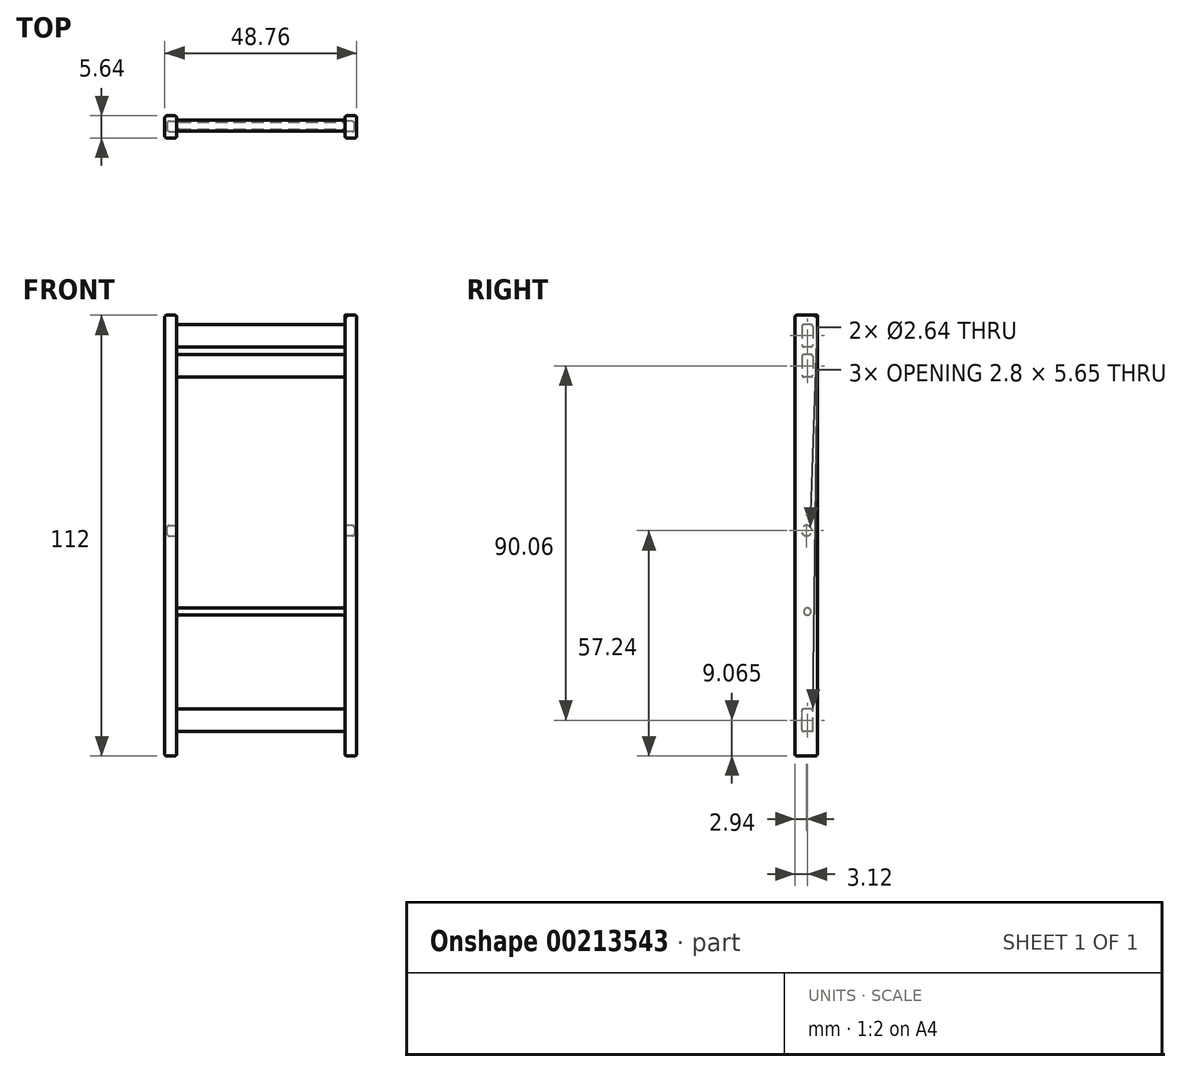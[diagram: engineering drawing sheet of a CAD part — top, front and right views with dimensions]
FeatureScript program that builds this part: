
annotation { "Feature Type Name" : "Feature", "Feature Type Description" : "" }
export const myFeature = defineFeature(function(context is Context, id is Id, definition is map)
    precondition{}
    {
        {
            var Q0;
            Q0=qCreatedBy(makeId("Right.planeOp"),FACE);
            var sketch = newSketch(context, id + "F0", { "sketchPlane" : qUnion([Q0])});
            skLineSegment(sketch, "E0.bottom", {"start": v(2.82, -56) * mm, "end": v(-2.82, -56) * mm});
            skLineSegment(sketch, "E0.top", {"start": v(2.82, 56) * mm, "end": v(-2.82, 56) * mm});
            skLineSegment(sketch, "E0.left", {"start": v(2.82, -56) * mm, "end": v(2.82, 56) * mm});
            skLineSegment(sketch, "E0.right", {"start": v(-2.82, -56) * mm, "end": v(-2.82, 56) * mm});
            skPoint(sketch, "E0.middle", {"position": v(0, 0) * mm});
            skSolve(sketch);
        }
        {
            var Q0;
            Q0=makeQuery(id+"F0.imprint","IMPRINT",FACE,{"disambiguationData":[TD([[makeQuery(id+"F0.imprint","IMPRINT",EDGE,{"derivedFrom":sQuery(id+"F0.wireOp",EDGE,"E0.bottom")}),-1.0]])]});
            extrude(context, id + "F1", {"entities" : qUnion([Q0]), "depth" : 3 * mm});
        }
        {
            var Q0;
            Q0=makeQuery(id+"F1.opExtrude","CAP_FACE",FACE,{"disambiguationData":[OSD([sQuery(id+"F0.wireOp",EDGE,"E0.bottom"),sQuery(id+"F0.wireOp",EDGE,"E0.top"),sQuery(id+"F0.wireOp",EDGE,"E0.left"),sQuery(id+"F0.wireOp",EDGE,"E0.right")])],"isStart":true});
            var sketch = newSketch(context, id + "F2", { "sketchPlane" : qUnion([Q0])});
            skLineSegment(sketch, "E1.bottom", {"start": v(-1.7, 53.6) * mm, "end": v(1.1, 53.6) * mm});
            skLineSegment(sketch, "E1.top", {"start": v(-1.7, 47.95) * mm, "end": v(1.1, 47.95) * mm});
            skLineSegment(sketch, "E1.left", {"start": v(-1.7, 53.6) * mm, "end": v(-1.7, 47.95) * mm});
            skLineSegment(sketch, "E1.right", {"start": v(1.1, 53.6) * mm, "end": v(1.1, 47.95) * mm});
            skLineSegment(sketch, "E2.bottom", {"start": v(-1.7, 45.95) * mm, "end": v(1.1, 45.95) * mm});
            skLineSegment(sketch, "E2.top", {"start": v(-1.7, 40.3) * mm, "end": v(1.1, 40.3) * mm});
            skLineSegment(sketch, "E2.left", {"start": v(-1.7, 45.95) * mm, "end": v(-1.7, 40.3) * mm});
            skLineSegment(sketch, "E2.right", {"start": v(1.1, 45.95) * mm, "end": v(1.1, 40.3) * mm});
            skLineSegment(sketch, "E3.bottom", {"start": v(-1.7, -49.76) * mm, "end": v(1.1, -49.76) * mm});
            skLineSegment(sketch, "E3.top", {"start": v(-1.7, -44.1) * mm, "end": v(1.1, -44.1) * mm});
            skLineSegment(sketch, "E3.left", {"start": v(-1.7, -49.76) * mm, "end": v(-1.7, -44.11) * mm});
            skLineSegment(sketch, "E3.right", {"start": v(1.1, -49.76) * mm, "end": v(1.1, -44.1) * mm});
            skCircle(sketch, "E4", {"center": v(-0.32, -19.3) * mm, "radius": 0.9 * mm});
            skSolve(sketch);
        }
        {
            var Q0;
            Q0 = qSketchRegion(id + "F2", true);
            extrude(context, id + "F3", {"entities" : qUnion([Q0]), "operationType" : NewBodyOperationType.ADD, "depth" : 42.76 * mm});
        }
        {
            var Q0;
            Q0=makeQuery(id+"F3.opExtrude","CAP_FACE",FACE,{"disambiguationData":[OSD([sQuery(id+"F2.wireOp",EDGE,"E1.bottom"),sQuery(id+"F2.wireOp",EDGE,"E1.top"),sQuery(id+"F2.wireOp",EDGE,"E1.left"),sQuery(id+"F2.wireOp",EDGE,"E1.right")])],"isStart":false});
            var sketch = newSketch(context, id + "F4", { "sketchPlane" : qUnion([Q0])});
            skLineSegment(sketch, "E5.bottom", {"start": v(-2.82, 56) * mm, "end": v(2.82, 56) * mm});
            skLineSegment(sketch, "E5.top", {"start": v(-2.82, -56) * mm, "end": v(2.82, -56) * mm});
            skLineSegment(sketch, "E5.left", {"start": v(-2.82, 56) * mm, "end": v(-2.82, -56) * mm});
            skLineSegment(sketch, "E5.right", {"start": v(2.82, 56) * mm, "end": v(2.82, -56) * mm});
            skSolve(sketch);
        }
        {
            var Q0;
            Q0 = qSketchRegion(id + "F4", true);
            extrude(context, id + "F5", {"entities" : qUnion([Q0]), "operationType" : NewBodyOperationType.ADD, "depth" : 3 * mm});
        }
        {
            var Q0;
            Q0=makeQuery(id+"F1.opExtrude","CAP_FACE",FACE,{"disambiguationData":[OSD([sQuery(id+"F0.wireOp",EDGE,"E0.bottom"),sQuery(id+"F0.wireOp",EDGE,"E0.top"),sQuery(id+"F0.wireOp",EDGE,"E0.left"),sQuery(id+"F0.wireOp",EDGE,"E0.right")])],"isStart":true});
            var sketch = newSketch(context, id + "F6", { "sketchPlane" : qUnion([Q0])});
            skCircle(sketch, "E6", {"center": v(-0.12, 1.24) * mm, "radius": 1.32 * mm});
            skLineSegment(sketch, "E7", {"start": v(0, 56) * mm, "end": v(0, -56) * mm, "construction": true});
            skSolve(sketch);
        }
        {
            var Q0;
            Q0=makeQuery(id+"F6.imprint","IMPRINT",FACE,{"disambiguationData":[TD([[makeQuery(id+"F6.imprint","IMPRINT",EDGE,{"derivedFrom":sQuery(id+"F6.wireOp",EDGE,"E6")}),1.0]])]});
            extrude(context, id + "F7", {"entities" : qUnion([Q0]), "operationType" : NewBodyOperationType.REMOVE, "oppositeDirection" : true, "depth" : 2.4 * mm});
        }
        {
            var Q0;
            Q0=makeQuery(id+"F5.opExtrude","CAP_FACE",FACE,{"disambiguationData":[OSD([sQuery(id+"F4.wireOp",EDGE,"E5.bottom"),sQuery(id+"F4.wireOp",EDGE,"E5.top"),sQuery(id+"F4.wireOp",EDGE,"E5.left"),sQuery(id+"F4.wireOp",EDGE,"E5.right")])],"isStart":true});
            var sketch = newSketch(context, id + "F8", { "sketchPlane" : qUnion([Q0])});
            skCircle(sketch, "E8", {"center": v(0.12, 1.24) * mm, "radius": 1.32 * mm});
            skSolve(sketch);
        }
        {
            var Q0;
            Q0 = qSketchRegion(id + "F8", true);
            extrude(context, id + "F9", {"entities" : qUnion([Q0]), "operationType" : NewBodyOperationType.REMOVE, "oppositeDirection" : true, "depth" : 2.4 * mm});
        }
        {
            var Q0;
            Q0=makeQuery(id+"F3.opExtrude","CAP_EDGE",EDGE,{"disambiguationData":[OSD([sQuery(id+"F2.wireOp",EDGE,"E2.top")])],"isStart":true});
            var Q1;
            Q1=makeQuery(id+"F3.opExtrude","CAP_EDGE",EDGE,{"disambiguationData":[OSD([sQuery(id+"F2.wireOp",EDGE,"E2.left")])],"isStart":true});
            var Q2;
            Q2=makeQuery(id+"F3.opExtrude","CAP_EDGE",EDGE,{"disambiguationData":[OSD([sQuery(id+"F2.wireOp",EDGE,"E1.top")])],"isStart":true});
            var Q3;
            Q3=makeQuery(id+"F3.opExtrude","CAP_EDGE",EDGE,{"disambiguationData":[OSD([sQuery(id+"F2.wireOp",EDGE,"E1.left")])],"isStart":true});
            var Q4;
            Q4=makeQuery(id+"F3.opExtrude","CAP_EDGE",EDGE,{"disambiguationData":[OSD([sQuery(id+"F2.wireOp",EDGE,"E1.bottom")])],"isStart":true});
            var Q5;
            Q5=makeQuery(id+"F3.opExtrude","CAP_EDGE",EDGE,{"disambiguationData":[OSD([sQuery(id+"F2.wireOp",EDGE,"E1.right")])],"isStart":true});
            var Q6;
            Q6=makeQuery(id+"F3.opExtrude","CAP_EDGE",EDGE,{"disambiguationData":[OSD([sQuery(id+"F2.wireOp",EDGE,"E2.bottom")])],"isStart":true});
            var Q7;
            Q7=makeQuery(id+"F3.opExtrude","CAP_EDGE",EDGE,{"disambiguationData":[OSD([sQuery(id+"F2.wireOp",EDGE,"E2.right")])],"isStart":true});
            var Q8;
            Q8=makeQuery(id+"F3.opExtrude","CAP_EDGE",EDGE,{"disambiguationData":[OSD([sQuery(id+"F2.wireOp",EDGE,"E1.right")])],"isStart":false});
            var Q9;
            Q9=makeQuery(id+"F3.opExtrude","CAP_EDGE",EDGE,{"disambiguationData":[OSD([sQuery(id+"F2.wireOp",EDGE,"E1.bottom")])],"isStart":false});
            var Q10;
            Q10=makeQuery(id+"F3.opExtrude","CAP_EDGE",EDGE,{"disambiguationData":[OSD([sQuery(id+"F2.wireOp",EDGE,"E2.bottom")])],"isStart":false});
            var Q11;
            Q11=makeQuery(id+"F3.opExtrude","CAP_EDGE",EDGE,{"disambiguationData":[OSD([sQuery(id+"F2.wireOp",EDGE,"E2.right")])],"isStart":false});
            var Q12;
            Q12=makeQuery(id+"F3.opExtrude","CAP_EDGE",EDGE,{"disambiguationData":[OSD([sQuery(id+"F2.wireOp",EDGE,"E1.left")])],"isStart":false});
            var Q13;
            Q13=makeQuery(id+"F3.opExtrude","CAP_EDGE",EDGE,{"disambiguationData":[OSD([sQuery(id+"F2.wireOp",EDGE,"E1.top")])],"isStart":false});
            var Q14;
            Q14=makeQuery(id+"F3.opExtrude","CAP_EDGE",EDGE,{"disambiguationData":[OSD([sQuery(id+"F2.wireOp",EDGE,"E2.left")])],"isStart":false});
            var Q15;
            Q15=makeQuery(id+"F3.opExtrude","CAP_EDGE",EDGE,{"disambiguationData":[OSD([sQuery(id+"F2.wireOp",EDGE,"E2.top")])],"isStart":false});
            var Q16;
            Q16=makeQuery(id+"F3.opExtrude","CAP_EDGE",EDGE,{"disambiguationData":[OSD([sQuery(id+"F2.wireOp",EDGE,"E3.bottom")])],"isStart":false});
            var Q17;
            Q17=makeQuery(id+"F3.opExtrude","CAP_EDGE",EDGE,{"disambiguationData":[OSD([sQuery(id+"F2.wireOp",EDGE,"E3.left")])],"isStart":false});
            var Q18;
            Q18=makeQuery(id+"F3.opExtrude","CAP_EDGE",EDGE,{"disambiguationData":[OSD([sQuery(id+"F2.wireOp",EDGE,"E3.bottom")])],"isStart":true});
            var Q19;
            Q19=makeQuery(id+"F3.opExtrude","CAP_EDGE",EDGE,{"disambiguationData":[OSD([sQuery(id+"F2.wireOp",EDGE,"E3.left")])],"isStart":true});
            var Q20;
            Q20=makeQuery(id+"F3.opExtrude","CAP_EDGE",EDGE,{"disambiguationData":[OSD([sQuery(id+"F2.wireOp",EDGE,"E3.right")])],"isStart":false});
            var Q21;
            Q21=makeQuery(id+"F3.opExtrude","CAP_EDGE",EDGE,{"disambiguationData":[OSD([sQuery(id+"F2.wireOp",EDGE,"E3.top")])],"isStart":false});
            var Q22;
            Q22=makeQuery(id+"F3.opExtrude","CAP_EDGE",EDGE,{"disambiguationData":[OSD([sQuery(id+"F2.wireOp",EDGE,"E3.right")])],"isStart":true});
            var Q23;
            Q23=makeQuery(id+"F3.opExtrude","CAP_EDGE",EDGE,{"disambiguationData":[OSD([sQuery(id+"F2.wireOp",EDGE,"E3.top")])],"isStart":true});
            var Q24;
            Q24=makeQuery(id+"F3.opExtrude","SWEPT_FACE",FACE,{"disambiguationData":[OSD([sQuery(id+"F2.wireOp",EDGE,"E4")])]});
            fillet(context, id + "F10", {"entities" : qUnion([Q0, Q1, Q2, Q3, Q4, Q5, Q6, Q7, Q8, Q9, Q10, Q11, Q12, Q13, Q14, Q15, Q16, Q17, Q18, Q19, Q20, Q21, Q22, Q23, Q24]), "radius" : 0.7 * mm, "tangentPropagation" : true, "allowEdgeOverflow" : false});
        }
        {
            var Q0;
            Q0=makeQuery(id+"F7.boolean.opBoolean","COPY",EDGE,{"derivedFrom":makeQuery(id+"F7.opExtrude","CAP_EDGE",EDGE,{"disambiguationData":[OSD([sQuery(id+"F6.wireOp",EDGE,"E6")])],"isStart":true})});
            var Q1;
            Q1=makeQuery(id+"F7.boolean.opBoolean","COPY",FACE,{"derivedFrom":makeQuery(id+"F7.opExtrude","CAP_FACE",FACE,{"disambiguationData":[OSD([sQuery(id+"F6.wireOp",EDGE,"E6")])],"isStart":false})});
            var Q2;
            Q2=makeQuery(id+"F9.boolean.opBoolean","COPY",EDGE,{"derivedFrom":makeQuery(id+"F9.opExtrude","CAP_EDGE",EDGE,{"disambiguationData":[OSD([sQuery(id+"F8.wireOp",EDGE,"E8")])],"isStart":true})});
            var Q3;
            Q3=makeQuery(id+"F9.boolean.opBoolean","COPY",EDGE,{"derivedFrom":makeQuery(id+"F9.opExtrude","CAP_EDGE",EDGE,{"disambiguationData":[OSD([sQuery(id+"F8.wireOp",EDGE,"E8")])],"isStart":false})});
            var Q4;
            Q4=makeQuery(id+"F1.opExtrude","CAP_FACE",FACE,{"disambiguationData":[OSD([sQuery(id+"F0.wireOp",EDGE,"E0.bottom"),sQuery(id+"F0.wireOp",EDGE,"E0.top"),sQuery(id+"F0.wireOp",EDGE,"E0.left"),sQuery(id+"F0.wireOp",EDGE,"E0.right")])],"isStart":false});
            var Q5;
            Q5=makeQuery(id+"F1.opExtrude","SWEPT_FACE",FACE,{"disambiguationData":[OSD([sQuery(id+"F0.wireOp",EDGE,"E0.right")])]});
            var Q6;
            Q6=makeQuery(id+"F5.opExtrude","SWEPT_FACE",FACE,{"disambiguationData":[OSD([sQuery(id+"F4.wireOp",EDGE,"E5.right")])]});
            var Q7;
            Q7=makeQuery(id+"F5.opExtrude","CAP_FACE",FACE,{"disambiguationData":[OSD([sQuery(id+"F4.wireOp",EDGE,"E5.bottom"),sQuery(id+"F4.wireOp",EDGE,"E5.top"),sQuery(id+"F4.wireOp",EDGE,"E5.left"),sQuery(id+"F4.wireOp",EDGE,"E5.right")])],"isStart":false});
            var Q8;
            Q8=makeQuery(id+"F3.opExtrude","SWEPT_EDGE",EDGE,{"disambiguationData":[OSD([sQuery(id+"F2.wireOp",EDGE,"E3.bottom"),sQuery(id+"F2.wireOp",EDGE,"E3.right")])]});
            var Q9;
            Q9=makeQuery(id+"F3.opExtrude","SWEPT_EDGE",EDGE,{"disambiguationData":[OSD([sQuery(id+"F2.wireOp",EDGE,"E3.bottom"),sQuery(id+"F2.wireOp",EDGE,"E3.left")])]});
            var Q10;
            Q10=makeQuery(id+"F3.opExtrude","SWEPT_EDGE",EDGE,{"disambiguationData":[OSD([sQuery(id+"F2.wireOp",EDGE,"E3.top"),sQuery(id+"F2.wireOp",EDGE,"E3.right")])]});
            var Q11;
            Q11=makeQuery(id+"F5.opExtrude","SWEPT_FACE",FACE,{"disambiguationData":[OSD([sQuery(id+"F4.wireOp",EDGE,"E5.top")])]});
            var Q12;
            Q12=makeQuery(id+"F1.opExtrude","SWEPT_FACE",FACE,{"disambiguationData":[OSD([sQuery(id+"F0.wireOp",EDGE,"E0.bottom")])]});
            var Q13;
            Q13=makeQuery(id+"F3.opExtrude","SWEPT_EDGE",EDGE,{"disambiguationData":[OSD([sQuery(id+"F2.wireOp",EDGE,"E3.top"),sQuery(id+"F2.wireOp",EDGE,"E3.left")])]});
            var Q14;
            Q14=makeQuery(id+"F5.opExtrude","SWEPT_FACE",FACE,{"disambiguationData":[OSD([sQuery(id+"F4.wireOp",EDGE,"E5.bottom")])]});
            var Q15;
            Q15=makeQuery(id+"F3.opExtrude","SWEPT_EDGE",EDGE,{"disambiguationData":[OSD([sQuery(id+"F2.wireOp",EDGE,"E1.bottom"),sQuery(id+"F2.wireOp",EDGE,"E1.left")])]});
            var Q16;
            Q16=makeQuery(id+"F3.opExtrude","SWEPT_EDGE",EDGE,{"disambiguationData":[OSD([sQuery(id+"F2.wireOp",EDGE,"E1.bottom"),sQuery(id+"F2.wireOp",EDGE,"E1.right")])]});
            var Q17;
            Q17=makeQuery(id+"F3.opExtrude","SWEPT_EDGE",EDGE,{"disambiguationData":[OSD([sQuery(id+"F2.wireOp",EDGE,"E1.top"),sQuery(id+"F2.wireOp",EDGE,"E1.left")])]});
            var Q18;
            Q18=makeQuery(id+"F3.opExtrude","SWEPT_EDGE",EDGE,{"disambiguationData":[OSD([sQuery(id+"F2.wireOp",EDGE,"E2.bottom"),sQuery(id+"F2.wireOp",EDGE,"E2.left")])]});
            var Q19;
            Q19=makeQuery(id+"F3.opExtrude","SWEPT_EDGE",EDGE,{"disambiguationData":[OSD([sQuery(id+"F2.wireOp",EDGE,"E2.top"),sQuery(id+"F2.wireOp",EDGE,"E2.left")])]});
            var Q20;
            Q20=makeQuery(id+"F3.opExtrude","SWEPT_EDGE",EDGE,{"disambiguationData":[OSD([sQuery(id+"F2.wireOp",EDGE,"E2.bottom"),sQuery(id+"F2.wireOp",EDGE,"E2.right")])]});
            var Q21;
            Q21=makeQuery(id+"F3.opExtrude","SWEPT_EDGE",EDGE,{"disambiguationData":[OSD([sQuery(id+"F2.wireOp",EDGE,"E2.top"),sQuery(id+"F2.wireOp",EDGE,"E2.right")])]});
            var Q22;
            Q22=makeQuery(id+"F3.opExtrude","SWEPT_EDGE",EDGE,{"disambiguationData":[OSD([sQuery(id+"F2.wireOp",EDGE,"E1.top"),sQuery(id+"F2.wireOp",EDGE,"E1.right")])]});
            fillet(context, id + "F11", {"entities" : qUnion([Q0, Q1, Q2, Q3, Q4, Q5, Q6, Q7, Q8, Q9, Q10, Q11, Q12, Q13, Q14, Q15, Q16, Q17, Q18, Q19, Q20, Q21, Q22]), "radius" : .5 * mm, "tangentPropagation" : true, "allowEdgeOverflow" : false});
        }
        {
            var Q0;
            Q0=makeQuery(id+"F1.opExtrude","CAP_EDGE",EDGE,{"disambiguationData":[OSD([sQuery(id+"F0.wireOp",EDGE,"E0.left")])],"isStart":true});
            var Q1;
            Q1=makeQuery(id+"F5.opExtrude","CAP_EDGE",EDGE,{"disambiguationData":[OSD([sQuery(id+"F4.wireOp",EDGE,"E5.left")])],"isStart":true});
            fillet(context, id + "F12", {"entities" : qUnion([Q0, Q1]), "radius" : .5 * mm, "tangentPropagation" : true, "allowEdgeOverflow" : false});
        }
    });
